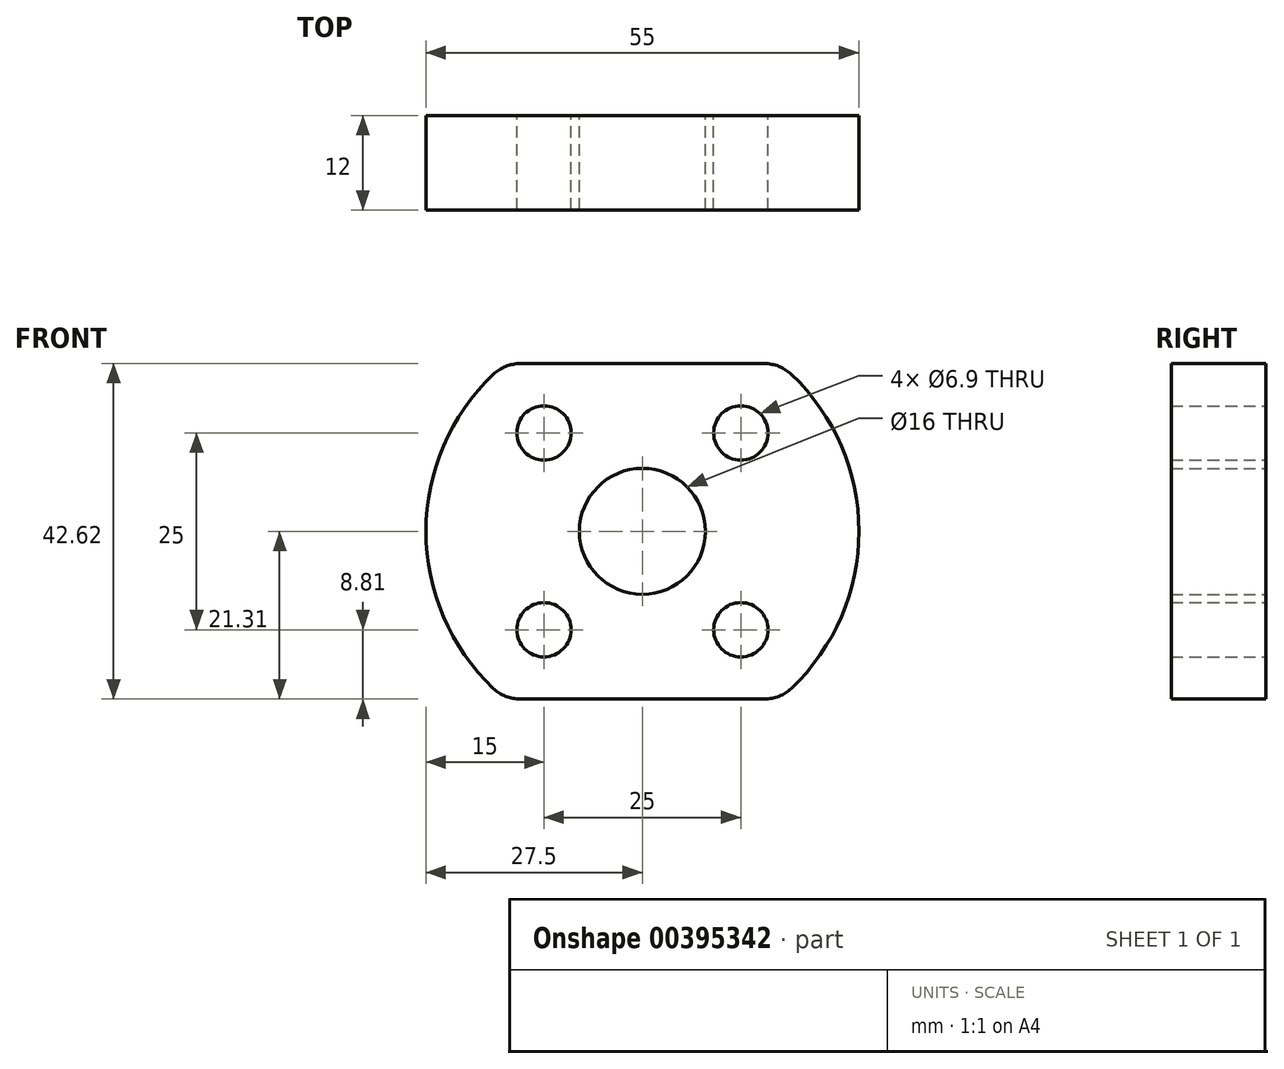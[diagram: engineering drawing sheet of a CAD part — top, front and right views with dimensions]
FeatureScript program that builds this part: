
annotation { "Feature Type Name" : "Feature", "Feature Type Description" : "" }
export const myFeature = defineFeature(function(context is Context, id is Id, definition is map)
    precondition{}
    {
        {
            var Q0;
            Q0=qCreatedBy(makeId("Front.planeOp"),FACE);
            var sketch = newSketch(context, id + "F0", { "sketchPlane" : qUnion([Q0])});
            skCircle(sketch, "E0", {"center": v(0, 0) * mm, "radius": 8 * mm});
            skArc(sketch, "E1", {"start": v(-17.38, 21.31) * mm, "mid": v(-27.5, 0) * mm, "end": v(-17.38, -21.31) * mm});
            skCircle(sketch, "E2", {"center": v(-12.5, 12.5) * mm, "radius": 3.45 * mm});
            skCircle(sketch, "E3", {"center": v(12.5, 12.5) * mm, "radius": 3.45 * mm});
            skCircle(sketch, "E4", {"center": v(-12.5, -12.5) * mm, "radius": 3.45 * mm});
            skCircle(sketch, "E5", {"center": v(12.5, -12.5) * mm, "radius": 3.45 * mm});
            skLineSegment(sketch, "E6.bottom", {"start": v(-17.38, 21.31) * mm, "end": v(17.38, 21.31) * mm});
            skLineSegment(sketch, "E6.top", {"start": v(-17.38, -21.31) * mm, "end": v(17.38, -21.31) * mm});
            skArc(sketch, "E7.trimOffspring", {"start": v(17.38, -21.31) * mm, "mid": v(27.5, 0) * mm, "end": v(17.38, 21.31) * mm});
            skSolve(sketch);
        }
        {
            var Q0;
            Q0 = qSketchRegion(id + "F0", true);
            extrude(context, id + "F1", {"entities" : qUnion([Q0]), "offsetDistance" : 25 * mm, "depth" : 12 * mm});
        }
        {
            var Q0;
            Q0=makeQuery(id+"F1.opExtrude","SWEPT_EDGE",EDGE,{"disambiguationData":[OSD([sQuery(id+"F0.wireOp",EDGE,"E1"),sQuery(id+"F0.wireOp",EDGE,"E6.bottom")])]});
            var Q1;
            Q1=makeQuery(id+"F1.opExtrude","SWEPT_EDGE",EDGE,{"disambiguationData":[OSD([sQuery(id+"F0.wireOp",EDGE,"E6.bottom"),sQuery(id+"F0.wireOp",EDGE,"E7.trimOffspring")])]});
            var Q2;
            Q2=makeQuery(id+"F1.opExtrude","SWEPT_EDGE",EDGE,{"disambiguationData":[OSD([sQuery(id+"F0.wireOp",EDGE,"E6.top"),sQuery(id+"F0.wireOp",EDGE,"E7.trimOffspring")])]});
            var Q3;
            Q3=makeQuery(id+"F1.opExtrude","SWEPT_EDGE",EDGE,{"disambiguationData":[OSD([sQuery(id+"F0.wireOp",EDGE,"E1"),sQuery(id+"F0.wireOp",EDGE,"E6.top")])]});
            fillet(context, id + "F2", {"entities" : qUnion([Q0, Q1, Q2, Q3]), "radius" : 5 * mm, "tangentPropagation" : true, "allowEdgeOverflow" : false});
        }
    });
